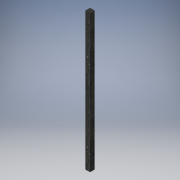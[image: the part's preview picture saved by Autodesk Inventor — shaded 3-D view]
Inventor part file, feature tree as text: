
AUTODESK INVENTOR PART (.ipt)
format: ipt  version: 2019 (Build 230136000, 136)  size: 99,328 bytes
history: native  units: mm
features: extrude x1, sketch x1
ambient origin geometry x8: Origin, YZ Plane, XZ Plane, XY Plane, X Axis, Y Axis, Z Axis, Center Point
bodies: Solid1 (feature_tree)
feature tree (2):
  extrude  "Extrusion1"  Depth=10.0mm
  sketch  "Sketch1"  dims[d0=310.0mm d1=10.0mm d2=198.4mm d3=10.0mm d4=10.0mm d5=0.0mm]
